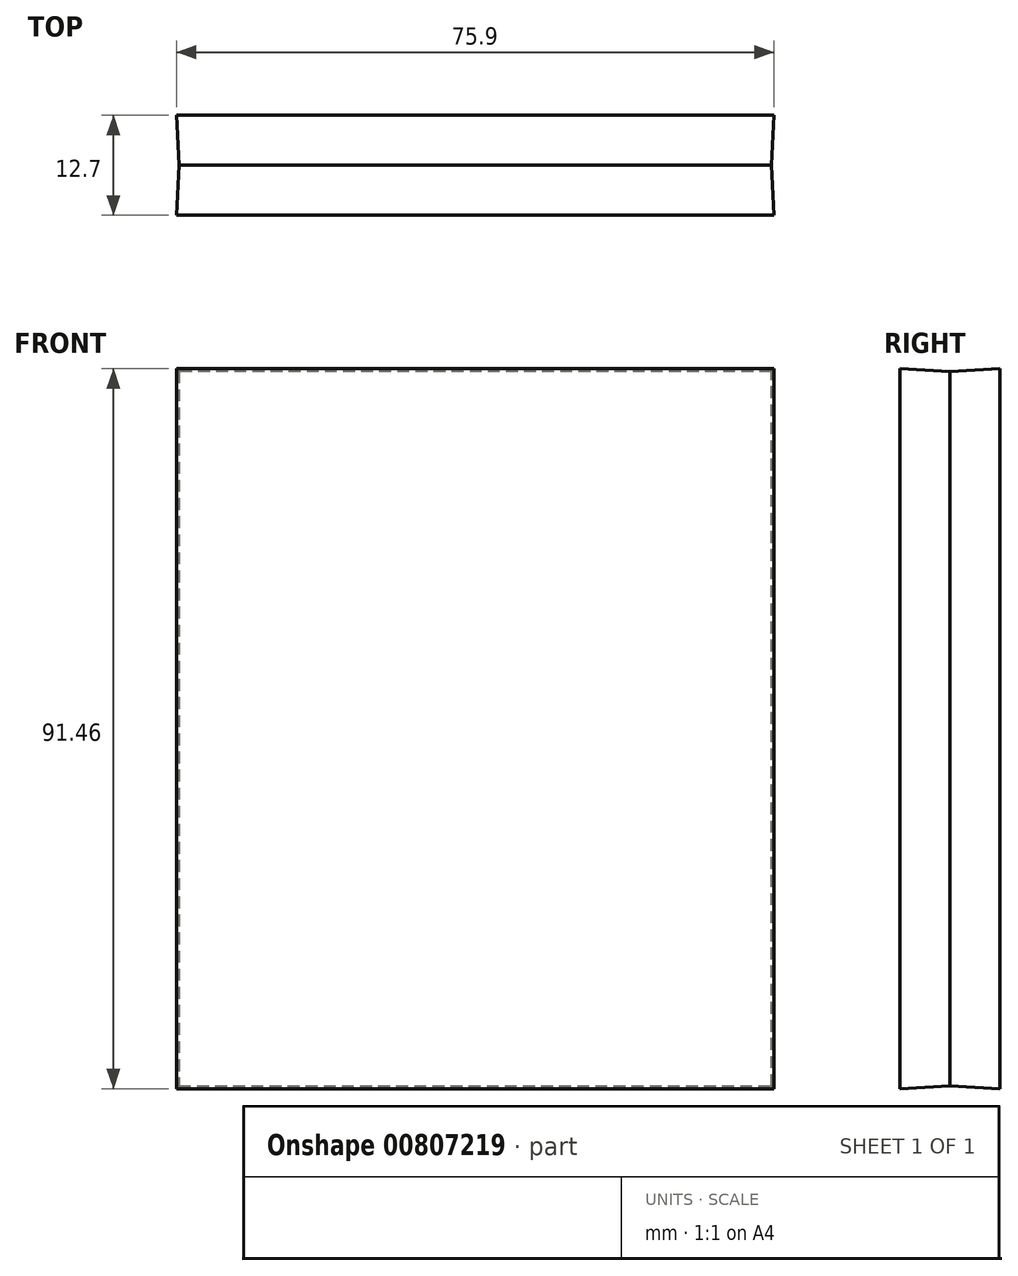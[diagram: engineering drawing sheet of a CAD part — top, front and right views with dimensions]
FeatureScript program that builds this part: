
annotation { "Feature Type Name" : "Feature", "Feature Type Description" : "" }
export const myFeature = defineFeature(function(context is Context, id is Id, definition is map)
    precondition{}
    {
        {
            var Q0;
            Q0=qCreatedBy(makeId("Front.planeOp"),FACE);
            var sketch = newSketch(context, id + "F0", { "sketchPlane" : qUnion([Q0])});
            skLineSegment(sketch, "E0.bottom", {"start": v(75.24, 90.8) * mm, "end": v(0, 90.8) * mm});
            skLineSegment(sketch, "E0.top", {"start": v(75.24, 0) * mm, "end": v(0, 0) * mm});
            skLineSegment(sketch, "E0.left", {"start": v(75.24, 90.8) * mm, "end": v(75.24, 0) * mm});
            skLineSegment(sketch, "E0.right", {"start": v(0, 90.8) * mm, "end": v(0, 0) * mm});
            skLineSegment(sketch, "E1.bottom", {"start": v(0, 0) * mm, "end": v(75.24, 0) * mm});
            skLineSegment(sketch, "E1.top", {"start": v(0, -68.86) * mm, "end": v(75.24, -68.86) * mm});
            skLineSegment(sketch, "E1.left", {"start": v(0, 0) * mm, "end": v(0, -68.86) * mm});
            skLineSegment(sketch, "E1.right", {"start": v(75.24, 0) * mm, "end": v(75.24, -68.86) * mm});
            skSolve(sketch);
        }
        {
            var Q0;
            Q0=makeQuery(id+"F0.imprint","IMPRINT",FACE,{"disambiguationData":[TD([[makeQuery(id+"F0.imprint","IMPRINT",EDGE,{"derivedFrom":sQuery(id+"F0.wireOp",EDGE,"E0.bottom")}),1.0]])]});
            extrude(context, id + "F1", {"entities" : qUnion([Q0]), "endBound" : BoundingType.SYMMETRIC, "oppositeDirection" : true, "depth" : 12.7 * mm, "offsetDistance" : 25.4 * mm, "hasDraft" : true, "draftAngle" : 3 * degree});
        }
    });
